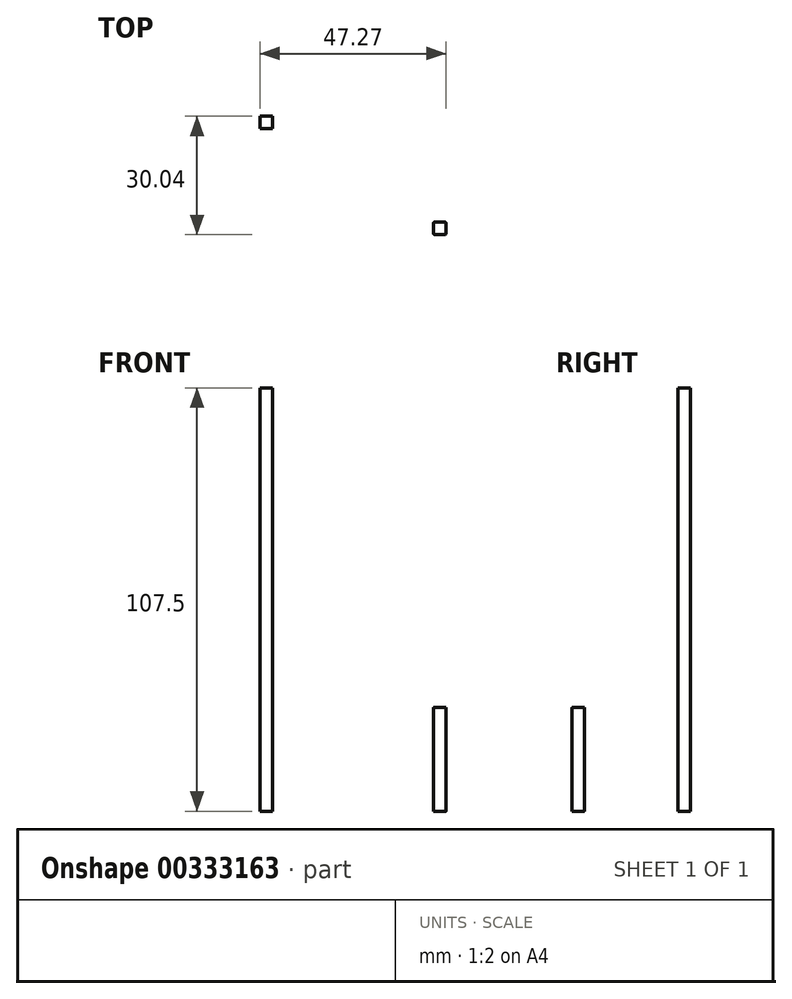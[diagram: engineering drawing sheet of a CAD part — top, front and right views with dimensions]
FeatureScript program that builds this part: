
annotation { "Feature Type Name" : "Feature", "Feature Type Description" : "" }
export const myFeature = defineFeature(function(context is Context, id is Id, definition is map)
    precondition{}
    {
        {
            var Q0;
            Q0=qCreatedBy(makeId("Top.planeOp"),FACE);
            var sketch = newSketch(context, id + "F0", { "sketchPlane" : qUnion([Q0])});
            skLineSegment(sketch, "E0.bottom", {"start": v(1.57, 1.58) * mm, "end": v(-1.58, 1.58) * mm});
            skLineSegment(sketch, "E0.top", {"start": v(1.58, -1.58) * mm, "end": v(-1.57, -1.58) * mm});
            skLineSegment(sketch, "E0.left", {"start": v(1.57, 1.58) * mm, "end": v(1.58, -1.58) * mm});
            skLineSegment(sketch, "E0.right", {"start": v(-1.58, 1.58) * mm, "end": v(-1.57, -1.58) * mm});
            skPoint(sketch, "E0.middle", {"position": v(0, 0) * mm});
            skLineSegment(sketch, "E1.bottom", {"start": v(-42.55, 28.47) * mm, "end": v(-45.7, 28.47) * mm});
            skLineSegment(sketch, "E1.top", {"start": v(-42.55, 25.32) * mm, "end": v(-45.7, 25.32) * mm});
            skLineSegment(sketch, "E1.left", {"start": v(-42.55, 28.47) * mm, "end": v(-42.55, 25.32) * mm});
            skLineSegment(sketch, "E1.right", {"start": v(-45.7, 28.47) * mm, "end": v(-45.7, 25.32) * mm});
            skPoint(sketch, "E1.middle", {"position": v(-44.12, 26.9) * mm});
            skSolve(sketch);
        }
        {
            var Q0;
            Q0=makeQuery(id+"F0.imprint","IMPRINT",FACE,{"disambiguationData":[TD([[makeQuery(id+"F0.imprint","IMPRINT",EDGE,{"derivedFrom":sQuery(id+"F0.wireOp",EDGE,"E0.bottom")}),1.0]])]});
            extrude(context, id + "F1", {"entities" : qUnion([Q0]), "depth" : 26.3 * mm});
        }
        {
            var Q0;
            Q0=makeQuery(id+"F1.opExtrude","SWEPT_EDGE",EDGE,{"disambiguationData":[OSD([sQuery(id+"F0.wireOp",EDGE,"E0.top"),sQuery(id+"F0.wireOp",EDGE,"E0.right")])]});
            var Q1;
            Q1=makeQuery(id+"F1.opExtrude","SWEPT_EDGE",EDGE,{"disambiguationData":[OSD([sQuery(id+"F0.wireOp",EDGE,"E0.top"),sQuery(id+"F0.wireOp",EDGE,"E0.left")])]});
            var Q2;
            Q2=makeQuery(id+"F1.opExtrude","SWEPT_EDGE",EDGE,{"disambiguationData":[OSD([sQuery(id+"F0.wireOp",EDGE,"E0.bottom"),sQuery(id+"F0.wireOp",EDGE,"E0.left")])]});
            var Q3;
            Q3=makeQuery(id+"F1.opExtrude","SWEPT_EDGE",EDGE,{"disambiguationData":[OSD([sQuery(id+"F0.wireOp",EDGE,"E0.bottom"),sQuery(id+"F0.wireOp",EDGE,"E0.right")])]});
            fillet(context, id + "F2", {"entities" : qUnion([Q0, Q1, Q2, Q3]), "radius" : 0.25 * mm, "tangentPropagation" : true, "allowEdgeOverflow" : false});
        }
        {
            var Q0;
            Q0=makeQuery(id+"F0.imprint","IMPRINT",FACE,{"disambiguationData":[TD([[makeQuery(id+"F0.imprint","IMPRINT",EDGE,{"derivedFrom":sQuery(id+"F0.wireOp",EDGE,"E1.bottom")}),1.0]])]});
            extrude(context, id + "F3", {"entities" : qUnion([Q0]), "depth" : 107.5 * mm});
        }
    });
